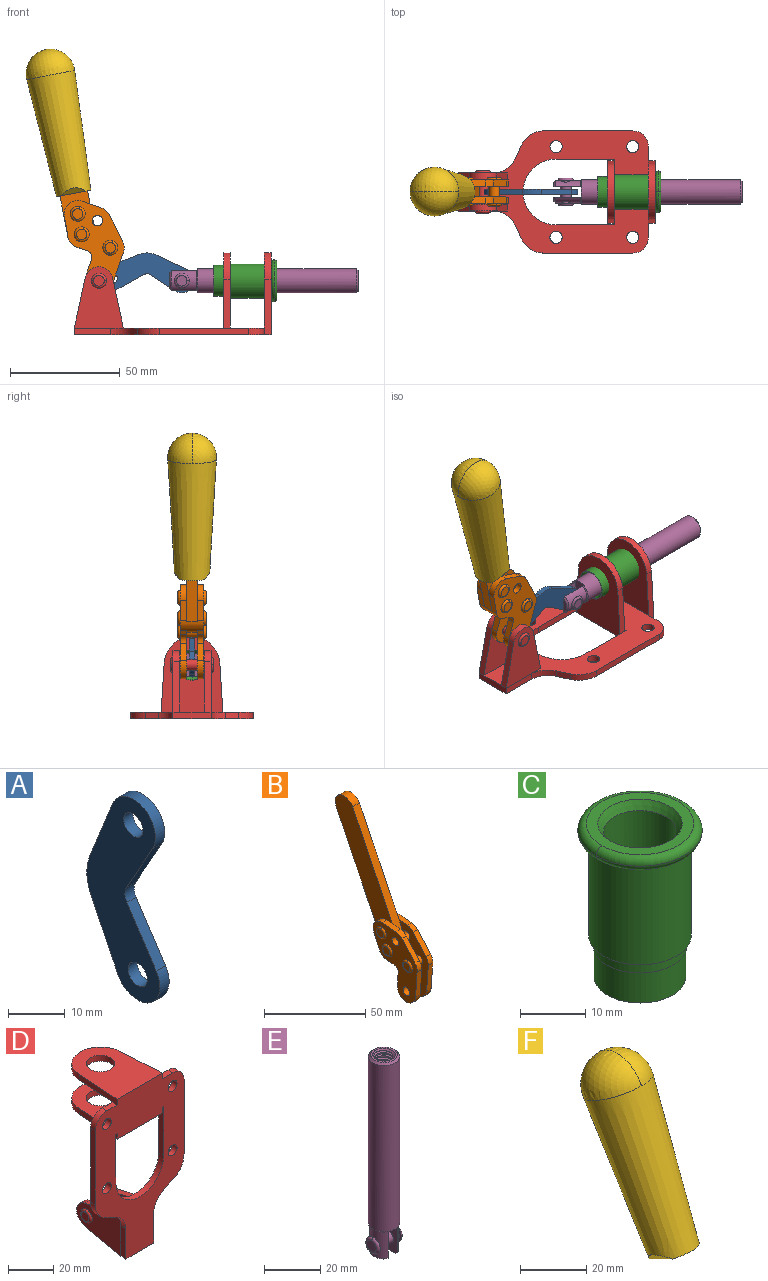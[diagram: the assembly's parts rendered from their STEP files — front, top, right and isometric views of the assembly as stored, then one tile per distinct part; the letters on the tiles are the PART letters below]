
ASSEMBLY  parts=6 mates=5
PART A: 12 faces, bbox 2.3x18.2x42.8 mm
  f0: cylinder r=2.4mm len=4.8mm, axis (1,0,0), area 34.9mm2, adj f4,f11
  f1: cylinder r=10.41mm len=8.47mm, axis (1,0,0), area 20.2mm2, adj f4,f9,f10,f11
  f2: cylinder r=3.05mm len=3.16mm, axis (1,0,0), area 7.7mm2, adj f4,f6,f7,f11
  f3: cylinder r=2.4mm len=4.8mm, axis (1,0,0), area 34.9mm2, adj f4,f11
  f4: plane 42.81x18.23mm, normal (-1,0,0), area 414.1mm2, adj f0,f1,f2,f3,f5,f6,f7,f8
  f5: cylinder r=5.54mm len=10.67mm, axis (1,0,0), area 41.8mm2, adj f4,f6,f10,f11
  f6: plane 11.66x6.53mm, normal (0,-0.87,-0.49), area 30.9mm2, adj f2,f4,f5,f11
  f7: plane 11.17x7.33mm, normal (0,-0.84,0.55), area 30.9mm2, adj f2,f4,f8,f11
  f8: cylinder r=5.54mm len=10.51mm, axis (1,0,0), area 41.8mm2, adj f4,f7,f9,f11
  f9: plane 13.67x6.67mm, normal (0,0.9,-0.44), area 35.1mm2, adj f1,f4,f8,f11
  f10: plane 14.1x5.7mm, normal (0,0.93,0.37), area 35.1mm2, adj f1,f4,f5,f11
  f11: plane 42.81x18.23mm, normal (1,0,0), area 414.1mm2, adj f0,f1,f2,f3,f5,f6,f7,f8
PART B: 59 faces, bbox 12.9x60.2x99.6 mm
  f0: torus R=2.39mm, axis (-1,0,0), area 14.9mm2, adj f20,f43,f51
  f1: torus R=2.39mm, axis (-1,0,0), area 14.9mm2, adj f19,f42,f51
  f2: torus R=2.39mm, axis (-1,0,0), area 14.9mm2, adj f18,f35,f51
  f3: torus R=2.39mm, axis (-1,0,0), area 14.9mm2, adj f14,f17,f23
  f4: torus R=2.39mm, axis (-1,0,0), area 14.9mm2, adj f13,f16,f23
  f5: torus R=2.39mm, axis (-1,0,0), area 14.9mm2, adj f12,f15,f23
  f6: cylinder r=2.39mm len=4.78mm, axis (1,0,0), area 46.5mm2, adj f48,f50,f51
  f7: cylinder r=2.39mm len=4.78mm, axis (1,0,0), area 46.5mm2, adj f50,f51
  f8: cylinder r=6.35mm len=12.68mm, axis (1,0,0), area 61.8mm2, adj f38,f39,f50,f51
  f9: cylinder r=2.39mm len=4.78mm, axis (-1,0,0), area 70.5mm2, adj f46,f50
  f10: cylinder r=2.39mm len=4.78mm, axis (-1,0,0), area 46.5mm2, adj f23,f45,f46
  f11: cylinder r=2.39mm len=4.78mm, axis (-1,0,0), area 46.5mm2, adj f23,f46
  f12: plane 4.78x4.78mm, normal (1,0,0), area 17.9mm2, adj f5,f15
  f13: plane 4.78x4.78mm, normal (1,0,0), area 17.9mm2, adj f4,f16
  f14: plane 4.78x4.78mm, normal (1,0,0), area 17.9mm2, adj f3,f17
  f15: torus R=2.39mm, axis (-1,0,0), area 14.9mm2, adj f5,f12,f23
  f16: torus R=2.39mm, axis (-1,0,0), area 14.9mm2, adj f4,f13,f23
  f17: torus R=2.39mm, axis (-1,0,0), area 14.9mm2, adj f3,f14,f23
  f18: plane 4.78x4.78mm, normal (-1,0,0), area 17.9mm2, adj f2,f35
  f19: plane 4.78x4.78mm, normal (-1,0,0), area 17.9mm2, adj f1,f42
  f20: plane 4.78x4.78mm, normal (-1,0,0), area 17.9mm2, adj f0,f43
  f21: plane 2.26x0.2mm, normal (1,0,0), area 0.2mm2, adj f31,f44
  f22: plane 2.26x0.2mm, normal (-1,0,0), area 0.2mm2, adj f41,f44
  f23: plane 39.37x30.77mm, normal (1,0,0), area 565.5mm2, adj f3,f4,f5,f10,f11,f15,f16,f17
  f24: cylinder r=6.1mm len=4.15mm, axis (-1,0,0), area 14.7mm2, adj f23,f25,f32,f46
  f25: plane 10.25x9.01mm, normal (0,-0.75,0.66), area 42.3mm2, adj f23,f24,f26,f46
  f26: cylinder r=6.35mm len=4.64mm, axis (-1,0,0), area 15.6mm2, adj f23,f25,f27,f46
  f27: plane 15.84x3.1mm, normal (0,-1,-0.07), area 49.2mm2, adj f23,f26,f28,f46
  f28: cylinder r=6.35mm len=12.68mm, axis (-1,0,0), area 61.8mm2, adj f23,f27,f29,f46
  f29: plane 8.11x3.1mm, normal (0,1,0.07), area 25.2mm2, adj f23,f28,f30,f46
  f30: cylinder r=3.05mm len=3.25mm, axis (-1,0,0), area 14.8mm2, adj f23,f29,f31,f46
  f31: plane 5.99x3.1mm, normal (0,0.07,-1), area 18.6mm2, adj f21,f23,f30,f44,f46
  f32: plane 9.5x3.1mm, normal (0,-0.07,1), area 29.5mm2, adj f23,f24,f33,f46,f47
  f33: cylinder r=6.1mm len=8.63mm, axis (-1,0,0), area 39.1mm2, adj f23,f32,f34,f47
  f34: plane 8.65x3.96mm, normal (0,0.91,-0.42), area 29.5mm2, adj f23,f33,f44,f47
  f35: torus R=2.39mm, axis (-1,0,0), area 14.9mm2, adj f2,f18,f51
  f36: plane 10.25x9.01mm, normal (0,-0.75,0.66), area 42.3mm2, adj f37,f49,f50,f51
  f37: cylinder r=6.35mm len=4.64mm, axis (1,0,0), area 15.6mm2, adj f36,f38,f50,f51
  f38: plane 15.84x3.1mm, normal (0,-1,-0.07), area 49.2mm2, adj f8,f37,f50,f51
  f39: plane 8.11x3.1mm, normal (0,1,0.07), area 25.2mm2, adj f8,f40,f50,f51
  f40: cylinder r=3.05mm len=3.25mm, axis (1,0,0), area 14.8mm2, adj f39,f41,f50,f51
  f41: plane 5.99x3.1mm, normal (0,0.07,-1), area 18.6mm2, adj f22,f40,f44,f50,f51
  f42: torus R=2.39mm, axis (-1,0,0), area 14.9mm2, adj f1,f19,f51
  f43: torus R=2.39mm, axis (-1,0,0), area 14.9mm2, adj f0,f20,f51
  f44: cylinder r=6.35mm len=12.12mm, axis (-1,0,0), area 128.9mm2, adj f21,f22,f23,f31,f34,f41,f46,f47
  f45: plane 2.65x1.35mm, normal (1,0,0), area 1mm2, adj f10,f55
  f46: plane 39.08x20.42mm, normal (-1,0,0), area 412.5mm2, adj f9,f10,f11,f24,f25,f26,f27,f28
  f47: plane 77.62x39.82mm, normal (1,0,0), area 850mm2, adj f32,f33,f34,f44,f53,f54,f55
  f48: plane 2.65x1.35mm, normal (-1,0,0), area 1mm2, adj f6,f55
  f49: cylinder r=6.1mm len=4.15mm, axis (1,0,0), area 14.7mm2, adj f36,f50,f51,f56
  f50: plane 39.08x20.42mm, normal (1,0,0), area 412.5mm2, adj f6,f7,f8,f9,f36,f37,f38,f39
  f51: plane 39.37x30.77mm, normal (-1,0,0), area 565.5mm2, adj f0,f1,f2,f6,f7,f8,f35,f36
  f52: plane 8.65x3.96mm, normal (0,0.91,-0.42), area 29.5mm2, adj f44,f51,f57,f58
  f53: plane 68.49x33.4mm, normal (0,0.9,-0.44), area 358.1mm2, adj f44,f47,f54,f58
  f54: cylinder r=6.35mm len=12.06mm, axis (1,0,0), area 93.7mm2, adj f47,f53,f55,f58
  f55: plane 68.49x33.4mm, normal (0,-0.9,0.44), area 358.1mm2, adj f44,f45,f46,f47,f48,f50,f54,f58
  f56: plane 9.5x3.1mm, normal (0,-0.07,1), area 29.5mm2, adj f49,f50,f51,f57,f58
  f57: cylinder r=6.1mm len=8.63mm, axis (1,0,0), area 39.1mm2, adj f51,f52,f56,f58
  f58: plane 77.62x39.82mm, normal (-1,0,0), area 850mm2, adj f44,f52,f53,f54,f55,f56,f57
PART C: 15 faces, bbox 20.6x20.6x28.7 mm
  f0: torus R=8.26mm, axis (0,0,1), area 56.8mm2, adj f1,f10,f12
  f1: torus R=8.26mm, axis (0,0,1), area 56.8mm2, adj f0,f6,f13
  f2: cylinder r=5.59mm len=25.91mm, axis (0,0,1), area 909.6mm2, adj f3,f4
  f3: cone r=6.86mm half-angle=45deg, axis (0,0,-1), area 70.2mm2, adj f2,f14
  f4: cone r=6.47mm half-angle=30deg, axis (0,0,1), area 66.7mm2, adj f2,f13
  f5: cylinder r=7.04mm len=14.07mm, axis (0,0,1), area 252.6mm2, adj f11,f14
  f6: torus R=8.26mm, axis (0,0,1), area 56.8mm2, adj f1,f12,f13
  f7: cylinder r=7.16mm len=14.33mm, axis (0,0,1), area 91.5mm2, adj f9,f11
  f8: cylinder r=7.86mm len=18.42mm, axis (0,0,1), area 909.6mm2, adj f9,f10
  f9: plane 15.72x15.72mm, normal (0,0,-1), area 33mm2, adj f7,f8
  f10: plane 16.51x16.51mm, normal (0,0,-1), area 19.9mm2, adj f0,f8,f12
  f11: plane 14.33x14.33mm, normal (0,0,-1), area 5.7mm2, adj f5,f7
  f12: torus R=8.26mm, axis (0,0,1), area 56.8mm2, adj f0,f6,f10
  f13: plane 16.51x16.51mm, normal (0,0,1), area 82.7mm2, adj f1,f4,f6
  f14: plane 14.07x14.07mm, normal (0,0,-1), area 7.8mm2, adj f3,f5
PART D: 55 faces, bbox 55.7x37.4x89.8 mm
  f0: torus R=2.41mm, axis (-1,0,0), area 15mm2, adj f11,f15,f25
  f1: torus R=2.41mm, axis (-1,0,0), area 15mm2, adj f10,f12,f22
  f2: cylinder r=2.78mm len=5.56mm, axis (0,-1,0), area 54.2mm2, adj f30,f54
  f3: cylinder r=14.99mm len=29.97mm, axis (0,-1,0), area 145.9mm2, adj f30,f49,f53,f54
  f4: cylinder r=2.78mm len=5.56mm, axis (0,-1,0), area 54.2mm2, adj f30,f54
  f5: cylinder r=2.78mm len=5.56mm, axis (0,-1,0), area 54.2mm2, adj f30,f54
  f6: cylinder r=2.78mm len=5.56mm, axis (0,-1,0), area 54.2mm2, adj f30,f54
  f7: cylinder r=6.35mm len=12.7mm, axis (0,0,1), area 123.6mm2, adj f27,f51
  f8: cylinder r=6.35mm len=12.7mm, axis (0,0,-1), area 124.7mm2, adj f21,f35
  f9: cylinder r=2.41mm len=11.18mm, axis (-1,0,0), area 169.4mm2, adj f16,f19
  f10: plane 4.83x4.83mm, normal (1,0,0), area 18.3mm2, adj f1,f12
  f11: plane 4.83x4.83mm, normal (-1,0,0), area 18.3mm2, adj f0,f15
  f12: torus R=2.41mm, axis (-1,0,0), area 15mm2, adj f1,f10,f22
  f13: cylinder r=6.35mm len=12.41mm, axis (1,0,0), area 53.4mm2, adj f18,f19,f22,f23
  f14: cylinder r=6.35mm len=12.41mm, axis (-1,0,0), area 53.4mm2, adj f16,f17,f24,f25
  f15: torus R=2.41mm, axis (-1,0,0), area 15mm2, adj f0,f11,f25
  f16: plane 27.86x22.35mm, normal (1,0,0), area 425.4mm2, adj f9,f14,f17,f24,f30
  f17: plane 22.86x4.97mm, normal (0,0.21,0.98), area 72.5mm2, adj f14,f16,f25,f30
  f18: plane 22.86x4.97mm, normal (0,0.21,0.98), area 72.5mm2, adj f13,f19,f22,f30
  f19: plane 27.86x22.35mm, normal (-1,0,0), area 425.4mm2, adj f9,f13,f18,f23,f30
  f20: cylinder r=12.7mm len=25.35mm, axis (0,0,-1), area 119.8mm2, adj f21,f34,f35,f36
  f21: plane 34.21x28.07mm, normal (0,0,-1), area 702.4mm2, adj f8,f20,f30,f34,f36
  f22: plane 27.96x22.45mm, normal (1,0,0), area 407.2mm2, adj f1,f12,f13,f18,f23,f30,f42,f43
  f23: plane 22.86x4.97mm, normal (0,0.21,-0.98), area 72.5mm2, adj f13,f19,f22,f44
  f24: plane 22.86x4.97mm, normal (0,0.21,-0.98), area 72.5mm2, adj f14,f16,f25,f44
  f25: plane 27.86x22.35mm, normal (-1,0,0), area 407.1mm2, adj f0,f14,f15,f17,f24,f30,f45,f46
  f26: plane 3.1x0.95mm, normal (0,0,-1), area 2.7mm2, adj f30,f49,f50,f54
  f27: plane 34.21x28.07mm, normal (0,0,1), area 702.4mm2, adj f7,f28,f30,f50,f52
  f28: cylinder r=12.7mm len=25.35mm, axis (0,0,1), area 118.8mm2, adj f27,f50,f51,f52
  f29: plane 3.1x0.95mm, normal (0,0,-1), area 2.7mm2, adj f30,f52,f53,f54
  f30: plane 86.54x55.63mm, normal (0,1,0), area 2362.9mm2, adj f2,f3,f4,f5,f6,f16,f17,f18
  f31: plane 40.56x3.1mm, normal (-1,0,0), area 125.7mm2, adj f30,f32,f48,f54
  f32: cylinder r=7.11mm len=7.11mm, axis (0,-1,0), area 34.6mm2, adj f30,f31,f33,f54
  f33: plane 6.67x3.1mm, normal (0,0,1), area 20.4mm2, adj f30,f32,f34,f54
  f34: plane 25.39x3.13mm, normal (-1,0.06,0), area 79.5mm2, adj f20,f21,f33,f35,f54
  f35: plane 37.31x28.45mm, normal (0,0,1), area 789.9mm2, adj f8,f20,f34,f36,f54
  f36: plane 25.39x3.13mm, normal (1,0.06,0), area 79.5mm2, adj f20,f21,f35,f37,f54
  f37: plane 6.67x3.1mm, normal (0,0,1), area 20.4mm2, adj f30,f36,f38,f54
  f38: cylinder r=7.11mm len=7.11mm, axis (0,-1,0), area 34.6mm2, adj f30,f37,f39,f54
  f39: plane 40.56x3.1mm, normal (1,0,0), area 125.7mm2, adj f30,f38,f40,f54
  f40: cylinder r=11.18mm len=10.16mm, axis (0,-1,0), area 39.5mm2, adj f30,f39,f41,f54
  f41: plane 6.09x3.1mm, normal (0.42,0,-0.91), area 20.8mm2, adj f30,f40,f42,f54
  f42: cylinder r=11.18mm len=9.41mm, axis (0,-1,0), area 37.2mm2, adj f22,f30,f41,f43,f54
  f43: plane 16.5x3.1mm, normal (1,0,0), area 51.1mm2, adj f22,f42,f44,f54
  f44: plane 17.37x3.1mm, normal (0,0,-1), area 53.8mm2, adj f23,f24,f30,f43,f45,f54
  f45: plane 16.5x3.1mm, normal (-1,0,0), area 51.1mm2, adj f25,f44,f46,f54
  f46: cylinder r=11.18mm len=9.41mm, axis (0,-1,0), area 37.2mm2, adj f25,f30,f45,f47,f54
  f47: plane 6.09x3.1mm, normal (-0.42,0,-0.91), area 20.8mm2, adj f30,f46,f48,f54
  f48: cylinder r=11.18mm len=10.16mm, axis (0,-1,0), area 39.5mm2, adj f30,f31,f47,f54
  f49: plane 26.54x3.1mm, normal (-1,0,0), area 82.3mm2, adj f3,f26,f30,f54
  f50: plane 25.39x3.1mm, normal (1,0.06,0), area 78.8mm2, adj f26,f27,f28,f51,f54
  f51: plane 37.31x28.45mm, normal (0,0,-1), area 789.9mm2, adj f7,f28,f50,f52,f54
  f52: plane 25.39x3.1mm, normal (-1,0.06,0), area 78.8mm2, adj f27,f28,f29,f51,f54
  f53: plane 26.54x3.1mm, normal (1,0,0), area 82.3mm2, adj f3,f29,f30,f54
  f54: plane 89.66x55.63mm, normal (0,-1,0), area 2678.5mm2, adj f2,f3,f4,f5,f6,f26,f29,f31
PART E: 48 faces, bbox 12.6x11.1x86.1 mm
  f0: torus R=2.41mm, axis (-1,0,0), area 15mm2, adj f30,f32,f34
  f1: torus R=2.41mm, axis (-1,0,0), area 15mm2, adj f29,f31,f33
  f2: cylinder r=5.54mm len=72.39mm, axis (0,0,1), area 2518.5mm2, adj f3,f4,f42,f43
  f3: cone r=5.54mm half-angle=45deg, axis (0,0,1), area 7.6mm2, adj f2,f5,f41
  f4: cone r=5.54mm half-angle=45deg, axis (0,0,-1), area 34.9mm2, adj f2,f39
  f5: cylinder r=5.08mm len=11.48mm, axis (0,0,1), area 108.3mm2, adj f3,f7,f8,f41
  f6: cylinder r=2.41mm len=4.83mm, axis (-1,0,0), area 71.2mm2, adj f40,f41
  f7: cylinder r=2.41mm len=4.83mm, axis (-1,0,0), area 7.6mm2, adj f5,f34
  f8: cone r=5.08mm half-angle=45deg, axis (0,0,1), area 10.6mm2, adj f5,f37,f41
  f9: cone r=3.98mm half-angle=45deg, axis (0,0,1), area 17.6mm2, adj f27,f39,f45,f46,f47
  f10: cylinder r=2.41mm len=4.83mm, axis (-1,0,0), area 7.6mm2, adj f33,f38
  f11: cylinder r=3.2mm len=6.4mm, axis (0,0,1), area 78.4mm2, adj f12,f28,f44,f45,f47
  f12: cylinder r=3.2mm len=6.4mm, axis (0,0,1), area 10.5mm2, adj f11,f13,f45,f47
  f13: cylinder r=3.2mm len=6.4mm, axis (0,0,1), area 10.5mm2, adj f12,f14,f45,f47
  f14: cylinder r=3.2mm len=6.4mm, axis (0,0,1), area 10.5mm2, adj f13,f15,f45,f47
  f15: cylinder r=3.2mm len=6.4mm, axis (0,0,1), area 10.5mm2, adj f14,f16,f45,f47
  f16: cylinder r=3.2mm len=6.4mm, axis (0,0,1), area 10.5mm2, adj f15,f17,f45,f47
  f17: cylinder r=3.2mm len=6.4mm, axis (0,0,1), area 10.5mm2, adj f16,f18,f45,f47
  f18: cylinder r=3.2mm len=6.4mm, axis (0,0,1), area 10.5mm2, adj f17,f19,f45,f47
  f19: cylinder r=3.2mm len=6.4mm, axis (0,0,1), area 10.5mm2, adj f18,f20,f45,f47
  f20: cylinder r=3.2mm len=6.4mm, axis (0,0,1), area 10.5mm2, adj f19,f21,f45,f47
  f21: cylinder r=3.2mm len=6.4mm, axis (0,0,1), area 10.5mm2, adj f20,f22,f45,f47
  f22: cylinder r=3.2mm len=6.4mm, axis (0,0,1), area 10.5mm2, adj f21,f23,f45,f47
  f23: cylinder r=3.2mm len=6.4mm, axis (0,0,1), area 10.5mm2, adj f22,f24,f45,f47
  f24: cylinder r=3.2mm len=6.4mm, axis (0,0,1), area 10.5mm2, adj f23,f25,f45,f47
  f25: cylinder r=3.2mm len=6.4mm, axis (0,0,1), area 10.5mm2, adj f24,f26,f45,f47
  f26: cylinder r=3.2mm len=6.4mm, axis (0,0,1), area 10.5mm2, adj f25,f27,f45,f47
  f27: cylinder r=3.2mm len=6.4mm, axis (0,0,1), area 7.4mm2, adj f9,f26,f45,f47
  f28: cone r=3.2mm half-angle=60deg, axis (0,0,1), area 37.2mm2, adj f11
  f29: plane 4.83x4.83mm, normal (-1,0,0), area 18.3mm2, adj f1,f31
  f30: plane 4.83x4.83mm, normal (1,0,0), area 18.3mm2, adj f0,f32
  f31: torus R=2.41mm, axis (-1,0,0), area 15mm2, adj f1,f29,f33
  f32: torus R=2.41mm, axis (-1,0,0), area 15mm2, adj f0,f30,f34
  f33: plane 6.83x6.83mm, normal (1,0,0), area 18.3mm2, adj f1,f10,f31
  f34: plane 6.83x6.83mm, normal (-1,0,0), area 18.3mm2, adj f0,f7,f32
  f35: cone r=5.08mm half-angle=45deg, axis (0,0,1), area 10.6mm2, adj f36,f38,f40
  f36: plane 7.25x1.97mm, normal (0,0,-1), area 10mm2, adj f35,f40
  f37: plane 7.25x1.97mm, normal (0,0,-1), area 10mm2, adj f8,f41
  f38: cylinder r=5.08mm len=11.48mm, axis (0,0,1), area 108.3mm2, adj f10,f35,f40,f42
  f39: plane 9.55x9.55mm, normal (0,0,1), area 22mm2, adj f4,f9
  f40: plane 12.76x10.09mm, normal (1,0,0), area 95.7mm2, adj f6,f35,f36,f38,f42,f43
  f41: plane 12.76x10.09mm, normal (-1,0,0), area 95.7mm2, adj f3,f5,f6,f8,f37,f43
  f42: cone r=5.54mm half-angle=45deg, axis (0,0,1), area 7.6mm2, adj f2,f38,f40
  f43: plane 11.07x4.7mm, normal (0,0,-1), area 50.4mm2, adj f2,f40,f41
  f44: plane 0.89x0.62mm, normal (-1,0,0), area 0.3mm2, adj f11,f45,f46,f47
  f45: bspline ~24.8x7.63mm, area 266.6mm2, adj f9,f11,f12,f13,f14,f15,f16,f17
  f46: bspline ~24.87x7.63mm, area 73.6mm2, adj f9,f44,f45,f47
  f47: bspline ~24.98x7.63mm, area 272.5mm2, adj f9,f11,f12,f13,f14,f15,f16,f17
PART F: 11 faces, bbox 22.3x42.6x64.5 mm
  f0: sphere r=11.13mm, area 411.4mm2, adj f1,f8
  f1: cone r=11.11mm half-angle=3.3deg, axis (0,0.44,0.9), area 3251.8mm2, adj f0,f7,f8,f9,f10
  f2: cylinder r=6.16mm len=11.7mm, axis (1,0,0), area 89.5mm2, adj f3,f4,f5,f6
  f3: plane 60.23x36.75mm, normal (-1,0,0), area 763.6mm2, adj f2,f4,f6,f10
  f4: plane 51.37x25.05mm, normal (0,0.9,-0.44), area 264.2mm2, adj f2,f3,f5,f10
  f5: plane 60.23x36.75mm, normal (1,0,0), area 763.6mm2, adj f2,f4,f6,f10
  f6: plane 51.37x25.05mm, normal (0,-0.9,0.44), area 264.2mm2, adj f2,f3,f5,f10
  f7: plane 9.95x5.95mm, normal (0.71,-0.31,-0.64), area 25.8mm2, adj f1,f10
  f8: sphere r=11.13mm, area 411.4mm2, adj f0,f1
  f9: plane 9.95x5.95mm, normal (-0.71,-0.31,-0.64), area 25.8mm2, adj f1,f10
  f10: plane 14.27x11.38mm, normal (0,-0.44,-0.9), area 106.7mm2, adj f1,f3,f4,f5,f6,f7,f9
PLACE A rot(axis=(0.58,-0.58,-0.58),120deg) t=(-46.79,1.32,1.22)mm
PLACE B rot(axis=(0.13,0.13,0.98),91deg) t=(-36.18,1.32,49.36)mm
PLACE C rot(axis=(0,1,0),90deg) t=(-36.16,-23.29,24.73)mm
PLACE D rot(axis=(0.58,0.58,0.58),120deg) t=(-36.16,1.32,0.12)mm fixed
PLACE E rot(axis=(-0.58,0.58,-0.58),120deg) t=(-46.01,1.32,49.34)mm
PLACE F rot(axis=(0.13,0.13,0.98),91deg) t=(-36.18,1.29,49.36)mm
MATE fastened C.f2 <-> D.f7  axis (1,0,0) through (10.23,1.32,24.73)mm
MATE revolute B.f7 <-> D.f0  axis (0,-1,0) through (-68.26,1.32,24.73)mm
MATE revolute A.f3 <-> E.f6  axis (0,-1,0) through (-30.54,1.32,24.73)mm
MATE slider E.f2 <-> C.f2  axis (1,0,0) through (12.77,1.32,24.73)mm
MATE fastened F.f2 <-> B.f54  axis (0,1,0) through (-90.62,-1.03,120.65)mm
